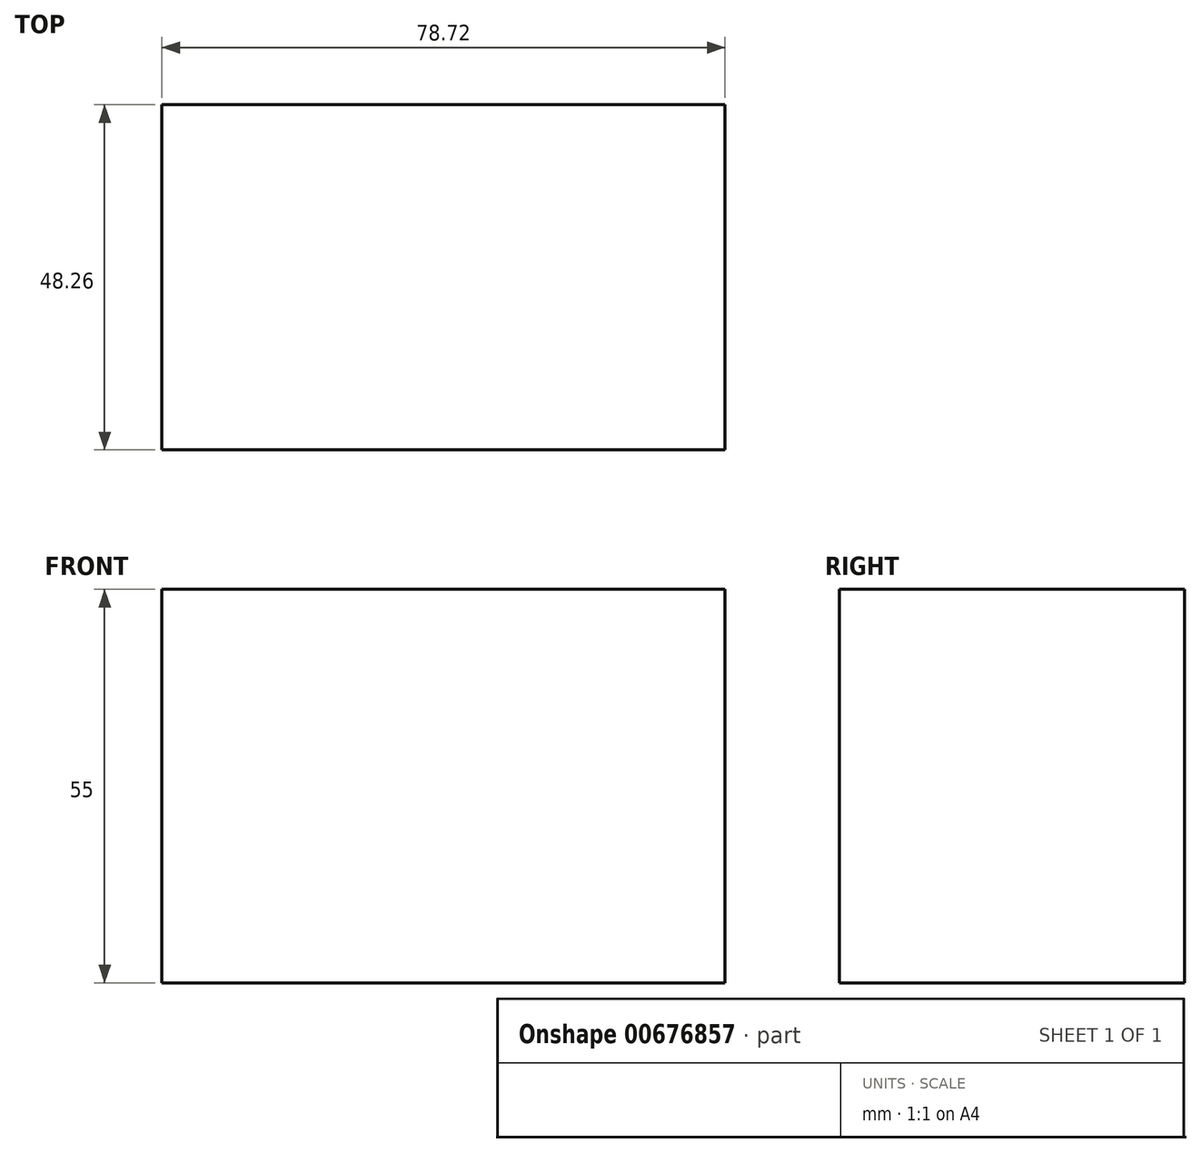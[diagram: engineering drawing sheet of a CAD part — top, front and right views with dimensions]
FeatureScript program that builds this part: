
annotation { "Feature Type Name" : "Feature", "Feature Type Description" : "" }
export const myFeature = defineFeature(function(context is Context, id is Id, definition is map)
    precondition{}
    {
        {
            var Q0;
            Q0=qCreatedBy(makeId("Top.planeOp"),FACE);
            var sketch = newSketch(context, id + "F0", { "sketchPlane" : qUnion([Q0])});
            skLineSegment(sketch, "E0.bottom", {"start": v(39.36, -24.13) * mm, "end": v(-39.36, -24.13) * mm});
            skLineSegment(sketch, "E0.top", {"start": v(39.36, 24.13) * mm, "end": v(-39.36, 24.13) * mm});
            skLineSegment(sketch, "E0.left", {"start": v(39.36, -24.13) * mm, "end": v(39.36, 24.13) * mm});
            skLineSegment(sketch, "E0.right", {"start": v(-39.36, -24.13) * mm, "end": v(-39.36, 24.13) * mm});
            skPoint(sketch, "E0.middle", {"position": v(0, 0) * mm});
            skSolve(sketch);
        }
        {
            var Q0;
            Q0 = qSketchRegion(id + "F0", true);
            extrude(context, id + "F1", {"entities" : qUnion([Q0]), "depth" : 25 * mm, "offsetDistance" : 25 * mm});
        }
        {
            var Q0;
            Q0=makeQuery(id+"F0.imprint","IMPRINT",FACE,{"disambiguationData":[TD([[makeQuery(id+"F0.imprint","IMPRINT",EDGE,{"derivedFrom":sQuery(id+"F0.wireOp",EDGE,"E0.bottom")}),-1.0]])]});
            extrude(context, id + "F2", {"entities" : qUnion([Q0]), "operationType" : NewBodyOperationType.ADD, "depth" : 25 * mm, "offsetDistance" : 25 * mm});
        }
        {
            var Q0;
            Q0=makeQuery(id+"F0.imprint","IMPRINT",FACE,{"disambiguationData":[TD([[makeQuery(id+"F0.imprint","IMPRINT",EDGE,{"derivedFrom":sQuery(id+"F0.wireOp",EDGE,"E0.bottom")}),-1.0]])]});
            extrude(context, id + "F3", {"entities" : qUnion([Q0]), "operationType" : NewBodyOperationType.ADD, "oppositeDirection" : true, "depth" : 30 * mm, "offsetDistance" : 25 * mm});
        }
    });
